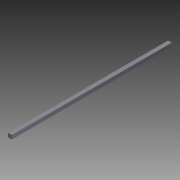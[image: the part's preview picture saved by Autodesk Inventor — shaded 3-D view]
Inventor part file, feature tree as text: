
AUTODESK INVENTOR PART (.ipt)
format: ipt  version: 2014 SP1 (Build 180222100, 222)  size: 173,056 bytes
history: native  units: in
note: dims shown in document units (in); Inventor stores cm internally (conversion verified against a paired STEP export)
features: projected_geometry x8, extrude x2, sketch x2, other x1, imported_body x1
ambient origin geometry x8: Origin, YZ Plane, XZ Plane, XY Plane, X Axis, Y Axis, Z Axis, Center Point
bodies: Body1 (feature_tree)
feature tree (14):
  parser-record x1  (decoder bookkeeping rows leaked as tree rows — omitted from the tree; the rows remain in map.json)
  imported_body  "Base1"
  extrude  "Extrusion1"  Depth=0.5in TaperAngle=0.0deg
  extrude  "Extrusion2"  [1 undecoded]
  sketch  "Sketch1"  dims[d0=6.5in d1=0.0in d2=0.5in d3=0.0in]
  projected_geometry  "Projected Loop1"
  projected_geometry  "Projected Loop2"
  projected_geometry  "Projected Loop3"
  projected_geometry  "Projected Loop4"
  projected_geometry  "Projected Loop5"
  projected_geometry  "Projected Loop6"
  projected_geometry  "Projected Loop7"
  projected_geometry  "Projected Loop8"
  sketch  "Sketch2"
note: 1 required parameter value undecoded (feature->parameter linkage not recoverable at this tier; creation-order binding heuristic only, values carry confidence <= 0.55)
